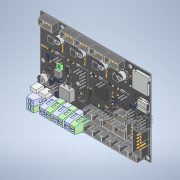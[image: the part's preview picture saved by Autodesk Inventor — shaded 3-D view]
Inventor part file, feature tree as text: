
AUTODESK INVENTOR PART (.ipt)
format: ipt  version: 2022 (Build 260153000, 153)  size: 26,429,440 bytes
history: native  units: in
note: dims shown in document units (in); Inventor stores cm internally (conversion verified against a paired STEP export)
features: other x489, extrude x194, fillet x4
ambient origin geometry x8: Origin, YZ Plane, XZ Plane, XY Plane, X Axis, Y Axis, Z Axis, Center Point
bodies: Solid1 (feature_tree), Solid2 (feature_tree), Solid3 (feature_tree), Solid4 (feature_tree), Solid5 (feature_tree), Solid6 (feature_tree), Solid7 (feature_tree), Solid8 (feature_tree), Solid9 (feature_tree), Solid10 (feature_tree), Solid11 (feature_tree), Solid12 (feature_tree), Solid13 (feature_tree), Solid14 (feature_tree), Solid15 (feature_tree), Solid16 (feature_tree), Solid17 (feature_tree), Solid18 (feature_tree), Solid19 (feature_tree), Solid20 (feature_tree), Solid21 (feature_tree), Solid22 (feature_tree), Solid23 (feature_tree), Solid24 (feature_tree), Solid25 (feature_tree), Solid26 (feature_tree), Solid27 (feature_tree), Solid28 (feature_tree), Solid29 (feature_tree), Solid30 (feature_tree), Solid31 (feature_tree), Solid32 (feature_tree), Solid33 (feature_tree), Solid34 (feature_tree), Solid35 (feature_tree), Solid36 (feature_tree), Solid37 (feature_tree), Solid38 (feature_tree), Solid39 (feature_tree), Solid40 (feature_tree), Solid41 (feature_tree), Solid42 (feature_tree), Solid43 (feature_tree), Solid44 (feature_tree), Solid45 (feature_tree), Solid46 (feature_tree), Solid47 (feature_tree), Solid48 (feature_tree), Solid49 (feature_tree), Solid50 (feature_tree), Solid51 (feature_tree), Solid52 (feature_tree), Solid53 (feature_tree), Solid54 (feature_tree), Solid55 (feature_tree), Solid56 (feature_tree), Solid57 (feature_tree), Solid58 (feature_tree), Solid59 (feature_tree), Solid60 (feature_tree), Solid61 (feature_tree), Solid62 (feature_tree), Solid63 (feature_tree), Solid64 (feature_tree), Solid65 (feature_tree), Solid66 (feature_tree), Solid67 (feature_tree), Solid68 (feature_tree), Solid69 (feature_tree), Solid70 (feature_tree), Solid71 (feature_tree), Solid72 (feature_tree), Solid73 (feature_tree), Solid74 (feature_tree), Solid75 (feature_tree), Solid76 (feature_tree), Solid77 (feature_tree), Solid78 (feature_tree), Solid79 (feature_tree), Solid80 (feature_tree), Solid81 (feature_tree), Solid82 (feature_tree), Solid83 (feature_tree), Solid84 (feature_tree), Solid85 (feature_tree), Solid86 (feature_tree), Solid87 (feature_tree), Solid88 (feature_tree), Solid89 (feature_tree), Solid90 (feature_tree), Solid91 (feature_tree), Solid92 (feature_tree), Solid93 (feature_tree), Solid94 (feature_tree), Solid95 (feature_tree), Solid96 (feature_tree), Solid97 (feature_tree), Solid98 (feature_tree), Solid99 (feature_tree), Solid100 (feature_tree), Solid101 (feature_tree), Solid102 (feature_tree), Solid103 (feature_tree), Solid104 (feature_tree), Solid105 (feature_tree), Solid106 (feature_tree), Solid107 (feature_tree), Solid108 (feature_tree), Solid109 (feature_tree), Solid110 (feature_tree), Solid111 (feature_tree), Solid112 (feature_tree), Solid113 (feature_tree), Solid114 (feature_tree), Solid115 (feature_tree), Solid116 (feature_tree), Solid117 (feature_tree), Solid118 (feature_tree), Solid119 (feature_tree), Solid120 (feature_tree), Solid121 (feature_tree), Solid122 (feature_tree), Solid123 (feature_tree), Solid124 (feature_tree), Solid125 (feature_tree), Solid126 (feature_tree), Solid127 (feature_tree), Solid128 (feature_tree), Solid129 (feature_tree), Solid130 (feature_tree), Solid131 (feature_tree), Solid132 (feature_tree), Solid133 (feature_tree), Solid134 (feature_tree), Solid135 (feature_tree), Solid136 (feature_tree), Solid137 (feature_tree), Solid138 (feature_tree), Solid139 (feature_tree), Solid140 (feature_tree), Solid141 (feature_tree), Solid142 (feature_tree), Solid143 (feature_tree), Solid144 (feature_tree), Solid145 (feature_tree), Solid146 (feature_tree), Solid147 (feature_tree), Solid148 (feature_tree), Solid149 (feature_tree), Solid150 (feature_tree), Solid151 (feature_tree), Solid152 (feature_tree), Solid153 (feature_tree), Solid154 (feature_tree), Solid155 (feature_tree), Solid156 (feature_tree), Solid157 (feature_tree), Solid158 (feature_tree), Solid159 (feature_tree), Solid160 (feature_tree), Solid161 (feature_tree), Solid162 (feature_tree), Solid163 (feature_tree), Solid164 (feature_tree), Solid165 (feature_tree), Solid166 (feature_tree), Solid167 (feature_tree), Solid168 (feature_tree), Solid169 (feature_tree), Solid170 (feature_tree), Solid171 (feature_tree), Solid172 (feature_tree), Solid173 (feature_tree), Solid174 (feature_tree), Solid175 (feature_tree), Solid176 (feature_tree), Solid177 (feature_tree), Solid178 (feature_tree), Solid179 (feature_tree), Solid180 (feature_tree), Solid181 (feature_tree), Solid182 (feature_tree), Solid183 (feature_tree), Solid184 (feature_tree), Solid185 (feature_tree), Solid186 (feature_tree), Solid187 (feature_tree), Solid188 (feature_tree), Solid189 (feature_tree), Solid190 (feature_tree), Solid191 (feature_tree), Solid192 (feature_tree), Solid193 (feature_tree), Solid194 (feature_tree), Solid195 (feature_tree), Solid196 (feature_tree), Solid197 (feature_tree), Solid198 (feature_tree), Solid199 (feature_tree), Solid200 (feature_tree), Solid201 (feature_tree), Solid202 (feature_tree), Solid203 (feature_tree), Solid204 (feature_tree), Solid205 (feature_tree), Solid206 (feature_tree), Solid207 (feature_tree), Solid208 (feature_tree), Solid209 (feature_tree), Solid210 (feature_tree), Solid211 (feature_tree), Solid212 (feature_tree), Solid213 (feature_tree), Solid214 (feature_tree), Solid215 (feature_tree), Solid216 (feature_tree), Solid217 (feature_tree), Solid218 (feature_tree), Solid219 (feature_tree), Solid220 (feature_tree), Solid221 (feature_tree), Solid222 (feature_tree), Solid223 (feature_tree), Solid224 (feature_tree), Solid225 (feature_tree), Solid226 (feature_tree), Solid227 (feature_tree), Solid228 (feature_tree), Solid229 (feature_tree), Solid230 (feature_tree), Solid231 (feature_tree), Solid232 (feature_tree), Solid233 (feature_tree), Solid234 (feature_tree), Solid235 (feature_tree), Solid236 (feature_tree), Solid237 (feature_tree), Solid238 (feature_tree), Solid239 (feature_tree), Solid240 (feature_tree), Solid241 (feature_tree), Solid242 (feature_tree), Solid243 (feature_tree), Solid244 (feature_tree), Solid245 (feature_tree), Solid246 (feature_tree), Solid247 (feature_tree), Solid248 (feature_tree), Solid249 (feature_tree), Solid250 (feature_tree), Solid251 (feature_tree), Solid252 (feature_tree), Solid253 (feature_tree), Solid254 (feature_tree), Solid255 (feature_tree), Solid256 (feature_tree), Solid257 (feature_tree), Solid258 (feature_tree), Solid259 (feature_tree), Solid260 (feature_tree), Solid261 (feature_tree), Solid262 (feature_tree), Solid263 (feature_tree), Solid264 (feature_tree), Solid265 (feature_tree), Solid266 (feature_tree), Solid267 (feature_tree), Solid268 (feature_tree), Solid269 (feature_tree), Solid270 (feature_tree), Solid271 (feature_tree), Solid272 (feature_tree), Solid273 (feature_tree), Solid274 (feature_tree), Solid275 (feature_tree), Solid276 (feature_tree), Solid277 (feature_tree), Solid278 (feature_tree), Solid279 (feature_tree), Solid280 (feature_tree), Solid281 (feature_tree), Solid282 (feature_tree), Solid283 (feature_tree), Solid284 (feature_tree), Solid285 (feature_tree), Solid286 (feature_tree), Solid287 (feature_tree), Solid288 (feature_tree), Solid289 (feature_tree), Solid290 (feature_tree), Solid291 (feature_tree), Solid292 (feature_tree), Solid293 (feature_tree), Solid294 (feature_tree), Solid295 (feature_tree), Solid296 (feature_tree), Solid297 (feature_tree), Solid298 (feature_tree), Solid299 (feature_tree), Solid300 (feature_tree), Solid301 (feature_tree), Solid302 (feature_tree), Solid303 (feature_tree), Solid304 (feature_tree), Solid305 (feature_tree), Solid306 (feature_tree), Solid307 (feature_tree), Solid308 (feature_tree), Solid309 (feature_tree), Solid310 (feature_tree), Solid311 (feature_tree), Solid312 (feature_tree), Solid313 (feature_tree), Solid314 (feature_tree), Solid315 (feature_tree), Solid316 (feature_tree), Solid317 (feature_tree), Solid318 (feature_tree), Solid319 (feature_tree), Solid320 (feature_tree), Solid321 (feature_tree), Solid322 (feature_tree), Solid323 (feature_tree), Solid324 (feature_tree), Solid325 (feature_tree), Solid326 (feature_tree), Solid327 (feature_tree), Solid328 (feature_tree), Solid329 (feature_tree), Solid330 (feature_tree), Solid331 (feature_tree), Solid332 (feature_tree), Solid333 (feature_tree), Solid334 (feature_tree), Solid335 (feature_tree), Solid336 (feature_tree), Solid337 (feature_tree), Solid338 (feature_tree), Solid339 (feature_tree), Solid340 (feature_tree), Solid341 (feature_tree), Solid342 (feature_tree), Solid343 (feature_tree), Solid344 (feature_tree), Solid345 (feature_tree), Solid346 (feature_tree), Solid347 (feature_tree), Solid348 (feature_tree), Solid349 (feature_tree), Solid350 (feature_tree), Solid351 (feature_tree), Solid352 (feature_tree), Solid353 (feature_tree), Solid354 (feature_tree), Solid355 (feature_tree), Solid356 (feature_tree), Solid357 (feature_tree), Solid358 (feature_tree), Solid359 (feature_tree), Solid360 (feature_tree), Solid361 (feature_tree), Solid362 (feature_tree), Solid363 (feature_tree), Solid364 (feature_tree), Solid365 (feature_tree), Solid366 (feature_tree), Solid367 (feature_tree), Solid368 (feature_tree), Solid369 (feature_tree), Solid370 (feature_tree), Solid371 (feature_tree), Solid372 (feature_tree), Solid373 (feature_tree), Solid374 (feature_tree), Solid375 (feature_tree), Solid376 (feature_tree), Solid377 (feature_tree), Solid378 (feature_tree), Solid379 (feature_tree), Solid380 (feature_tree), Solid381 (feature_tree), Solid382 (feature_tree), Solid383 (feature_tree), Solid384 (feature_tree), Solid385 (feature_tree), Solid386 (feature_tree), Solid387 (feature_tree), Solid388 (feature_tree), Solid389 (feature_tree), Solid390 (feature_tree), Solid391 (feature_tree), Solid392 (feature_tree), Solid393 (feature_tree), Solid394 (feature_tree), Solid395 (feature_tree), Solid396 (feature_tree), Solid397 (feature_tree), Solid398 (feature_tree), Solid399 (feature_tree), Solid400 (feature_tree), Solid401 (feature_tree), Solid402 (feature_tree), Solid403 (feature_tree), Solid404 (feature_tree), Solid405 (feature_tree), Solid406 (feature_tree), Solid407 (feature_tree), Solid408 (feature_tree), Solid409 (feature_tree), Solid410 (feature_tree), Solid411 (feature_tree), Solid412 (feature_tree), Solid413 (feature_tree), Solid414 (feature_tree), Solid415 (feature_tree), Solid416 (feature_tree), Solid417 (feature_tree), Solid418 (feature_tree), Solid419 (feature_tree), Solid420 (feature_tree), Solid421 (feature_tree), Solid422 (feature_tree), Solid423 (feature_tree), Solid424 (feature_tree), Solid425 (feature_tree), Solid426 (feature_tree), Solid427 (feature_tree), Solid428 (feature_tree), Solid429 (feature_tree), Solid430 (feature_tree), Solid431 (feature_tree), Solid432 (feature_tree), Solid433 (feature_tree), Solid434 (feature_tree), Solid435 (feature_tree), Solid436 (feature_tree), Solid437 (feature_tree), Solid438 (feature_tree), Solid439 (feature_tree), Solid440 (feature_tree), Solid441 (feature_tree), Solid442 (feature_tree), Solid443 (feature_tree), Solid444 (feature_tree), Solid445 (feature_tree), Solid446 (feature_tree), Solid447 (feature_tree), Solid448 (feature_tree), Solid449 (feature_tree), Solid450 (feature_tree), Solid451 (feature_tree), Solid452 (feature_tree), Solid453 (feature_tree), Solid454 (feature_tree), Solid455 (feature_tree), Solid456 (feature_tree), Solid457 (feature_tree), Solid458 (feature_tree), Solid459 (feature_tree), Solid460 (feature_tree), Solid461 (feature_tree), Solid462 (feature_tree), Solid463 (feature_tree), Solid464 (feature_tree), Solid465 (feature_tree), Solid466 (feature_tree), Solid467 (feature_tree), Solid468 (feature_tree), Solid469 (feature_tree), Solid470 (feature_tree), Solid471 (feature_tree), Solid472 (feature_tree), Solid473 (feature_tree), Solid474 (feature_tree), Solid475 (feature_tree), Solid476 (feature_tree), Solid477 (feature_tree), Solid478 (feature_tree), Solid479 (feature_tree), Solid480 (feature_tree), Solid481 (feature_tree), Solid482 (feature_tree), Solid483 (feature_tree), Solid484 (feature_tree), Solid485 (feature_tree), Solid486 (feature_tree), Solid487 (feature_tree), Solid488 (feature_tree), Solid489 (feature_tree), Solid490 (feature_tree), Solid491 (feature_tree), Solid492 (feature_tree), Solid493 (feature_tree), Solid494 (feature_tree), Solid495 (feature_tree), Solid496 (feature_tree), Solid497 (feature_tree), Solid498 (feature_tree), Solid499 (feature_tree), Solid500 (feature_tree), Solid501 (feature_tree), Solid502 (feature_tree), Solid503 (feature_tree), Solid504 (feature_tree), Solid505 (feature_tree), Solid506 (feature_tree), Solid507 (feature_tree), Solid508 (feature_tree), Solid509 (feature_tree), Solid510 (feature_tree), Solid511 (feature_tree), Solid512 (feature_tree), Solid513 (feature_tree), Solid514 (feature_tree), Solid515 (feature_tree), Solid516 (feature_tree), Solid517 (feature_tree), Solid518 (feature_tree), Solid519 (feature_tree), Solid520 (feature_tree), Solid521 (feature_tree), Solid522 (feature_tree), Solid523 (feature_tree), Solid524 (feature_tree), Solid525 (feature_tree), Solid526 (feature_tree), Solid527 (feature_tree), Solid528 (feature_tree), Solid529 (feature_tree), Solid530 (feature_tree), Solid531 (feature_tree), Solid532 (feature_tree), Solid533 (feature_tree), Solid534 (feature_tree), Solid535 (feature_tree), Solid536 (feature_tree), Solid537 (feature_tree), Solid538 (feature_tree), Solid539 (feature_tree), Solid540 (feature_tree), Solid541 (feature_tree), Solid542 (feature_tree), Solid543 (feature_tree), Solid544 (feature_tree), Solid545 (feature_tree), Solid546 (feature_tree), Solid547 (feature_tree), Solid548 (feature_tree), Solid549 (feature_tree), Solid550 (feature_tree), Solid551 (feature_tree), Solid552 (feature_tree), Solid553 (feature_tree), Solid554 (feature_tree), Solid555 (feature_tree), Solid556 (feature_tree), Solid557 (feature_tree), Solid558 (feature_tree), Solid559 (feature_tree), Solid560 (feature_tree), Solid561 (feature_tree), Solid562 (feature_tree), Solid563 (feature_tree), Solid564 (feature_tree), Solid565 (feature_tree), Solid566 (feature_tree), Solid567 (feature_tree), Solid568 (feature_tree), Solid569 (feature_tree), Solid570 (feature_tree), Solid571 (feature_tree), Solid572 (feature_tree), Solid573 (feature_tree), Solid574 (feature_tree), Solid575 (feature_tree), Solid576 (feature_tree), Solid577 (feature_tree), Solid578 (feature_tree), Solid579 (feature_tree), Solid580 (feature_tree), Solid581 (feature_tree), Solid582 (feature_tree), Solid583 (feature_tree), Solid584 (feature_tree), Solid585 (feature_tree), Solid586 (feature_tree), Solid587 (feature_tree), Solid588 (feature_tree), Solid589 (feature_tree), Solid590 (feature_tree), Solid591 (feature_tree), Solid592 (feature_tree), Solid593 (feature_tree), Solid594 (feature_tree), Solid595 (feature_tree), Solid596 (feature_tree), Solid597 (feature_tree), Solid598 (feature_tree), Solid599 (feature_tree), Solid600 (feature_tree), Solid601 (feature_tree), Solid602 (feature_tree), Solid603 (feature_tree), Solid604 (feature_tree), Solid605 (feature_tree), Solid606 (feature_tree), Solid607 (feature_tree), Solid608 (feature_tree), Solid609 (feature_tree), Solid610 (feature_tree), Solid611 (feature_tree), Solid612 (feature_tree), Solid613 (feature_tree), Solid614 (feature_tree), Solid615 (feature_tree), Solid616 (feature_tree), Solid617 (feature_tree), Solid618 (feature_tree), Solid619 (feature_tree), Solid620 (feature_tree), Solid621 (feature_tree), Solid622 (feature_tree), Solid623 (feature_tree), Solid624 (feature_tree), Solid625 (feature_tree), Solid626 (feature_tree), Solid627 (feature_tree), Solid628 (feature_tree), Solid629 (feature_tree), Solid630 (feature_tree), Solid631 (feature_tree), Solid632 (feature_tree), Solid633 (feature_tree), Solid634 (feature_tree), Solid635 (feature_tree), Solid636 (feature_tree), Solid637 (feature_tree), Solid638 (feature_tree), Solid639 (feature_tree), Solid640 (feature_tree), Solid641 (feature_tree), Solid642 (feature_tree), Solid643 (feature_tree), Solid644 (feature_tree), Solid645 (feature_tree), Solid646 (feature_tree), Solid647 (feature_tree), Solid648 (feature_tree), Solid649 (feature_tree), Solid650 (feature_tree), Solid651 (feature_tree), Solid652 (feature_tree), Solid653 (feature_tree), Solid654 (feature_tree), Solid655 (feature_tree), Solid656 (feature_tree), Solid657 (feature_tree), Solid658 (feature_tree), Solid659 (feature_tree), Solid660 (feature_tree), Solid661 (feature_tree), Solid662 (feature_tree), Solid663 (feature_tree), Solid664 (feature_tree), Solid665 (feature_tree), Solid666 (feature_tree), Solid667 (feature_tree), Solid668 (feature_tree), Solid669 (feature_tree), Solid670 (feature_tree), Solid671 (feature_tree), Solid672 (feature_tree), Solid673 (feature_tree), Solid674 (feature_tree), Solid675 (feature_tree), Solid676 (feature_tree), Solid677 (feature_tree), Solid678 (feature_tree), Solid679 (feature_tree), Solid680 (feature_tree), Solid681 (feature_tree), Solid682 (feature_tree), Solid683 (feature_tree), Solid684 (feature_tree), Solid685 (feature_tree), Solid686 (feature_tree), Solid687 (feature_tree), Solid688 (feature_tree), Solid689 (feature_tree), Solid690 (feature_tree), Solid691 (feature_tree), Solid692 (feature_tree), Solid693 (feature_tree), Solid694 (feature_tree), Solid695 (feature_tree), Solid696 (feature_tree), Solid697 (feature_tree), Solid698 (feature_tree), Solid699 (feature_tree), Solid700 (feature_tree), Solid701 (feature_tree), Solid702 (feature_tree), Solid703 (feature_tree), Solid704 (feature_tree), Solid705 (feature_tree), Solid706 (feature_tree), Solid707 (feature_tree), Solid708 (feature_tree), Solid709 (feature_tree), Solid710 (feature_tree), Solid711 (feature_tree), Solid712 (feature_tree), Solid713 (feature_tree), Solid714 (feature_tree), Solid715 (feature_tree), Solid716 (feature_tree), Solid717 (feature_tree), Solid718 (feature_tree), Solid719 (feature_tree), Solid720 (feature_tree), Solid721 (feature_tree), Solid722 (feature_tree), Solid723 (feature_tree), Solid724 (feature_tree), Solid725 (feature_tree), Solid726 (feature_tree), Solid727 (feature_tree), Solid728 (feature_tree), Solid729 (feature_tree), Solid730 (feature_tree), Solid731 (feature_tree), Solid732 (feature_tree), Solid733 (feature_tree), Solid734 (feature_tree), Solid735 (feature_tree), Solid736 (feature_tree), Solid737 (feature_tree), Solid738 (feature_tree), Solid739 (feature_tree), Solid740 (feature_tree), Solid741 (feature_tree), Solid742 (feature_tree), Solid743 (feature_tree), Solid744 (feature_tree), Solid745 (feature_tree), Solid746 (feature_tree), Solid747 (feature_tree), Solid748 (feature_tree), Solid749 (feature_tree), Solid750 (feature_tree), Solid751 (feature_tree), Solid752 (feature_tree), Solid753 (feature_tree), Solid754 (feature_tree), Solid755 (feature_tree), Solid756 (feature_tree), Solid757 (feature_tree), Solid758 (feature_tree), Solid759 (feature_tree), Solid760 (feature_tree)
feature tree (687):
  other  "Board_1:1"
  other  "KF128_1:1"
  other  "KF128_1:2"
  other  "KF128_1:3"
  other  "KF128_1:4"
  other  "KF128_1:5"
  other  "KF128_1:6"
  other  "KF128_1:7"
  other  "KF128_1:8"
  extrude  "Extruded_1:1"  [1 undecoded]
  extrude  "Extruded (1)_1:1"  [1 undecoded]
  extrude  "Extruded (1)_1:2"  [1 undecoded]
  extrude  "Extruded_1:2"  [1 undecoded]
  extrude  "Extruded (1)_1:3"  [1 undecoded]
  extrude  "Extruded (1)_1:4"  [1 undecoded]
  extrude  "Extruded (2)_1:1"  [1 undecoded]
  extrude  "Extruded (3)_1:1"  [1 undecoded]
  extrude  "Extruded (3)_1:2"  [1 undecoded]
  other  "KF128_2:1"
  other  "KF128_2:2"
  other  "KF128_2:3"
  other  "KF128_2:4"
  other  "KF128_2:5"
  other  "KF128_2:6"
  other  "KF128_2:7"
  other  "KF128_2:8"
  extrude  "Extruded (4)_1:1"  [1 undecoded]
  extrude  "Extruded (5)_1:1"  [1 undecoded]
  extrude  "Extruded (6)_1:1"  [1 undecoded]
  extrude  "Extruded (7)_1:1"  [1 undecoded]
  extrude  "Extruded (8)_1:1"  [1 undecoded]
  other  "Cylinder_1:1"
  other  "Cylinder_1:2"
  other  "Cylinder_1:3"
  other  "Cylinder_1:4"
  extrude  "Extruded (9)_1:1"  [1 undecoded]
  other  "usb_b-c_1:1"
  other  "usb_b-c_1:2"
  other  "usb_b-c_1:3"
  other  "usb_b-c_1:4"
  other  "usb_b-c_1:5"
  other  "usb_b-c_1:6"
  other  "User_Library-XH2_54_2PIN_RGB0_1:1"
  other  "User_Library-XH2_54_2PIN_RGB0_1:2"
  other  "User_Library-XH2_54_2PIN_RGB0_1:3"
  other  "User_Library-XH2_54_2PIN_RGB0_1:4"
  other  "User_Library-XH2_54_2PIN_RGB0_1:5"
  other  "User_Library-XH2_54_2PIN_RGB0_2:1"
  other  "User_Library-XH2_54_2PIN_RGB0_2:2"
  other  "User_Library-XH2_54_2PIN_RGB0_2:3"
  other  "User_Library-XH2_54_2PIN_RGB0_2:4"
  other  "User_Library-XH2_54_2PIN_RGB0_2:5"
  other  "Fusion_1:1"
  other  "Fusion_1:2"
  other  "Fusion_1:3"
  other  "Fusion_1:4"
  other  "Fusion_1:5"
  other  "Fusion_1:6"
  other  "Fusion_1:7"
  other  "Fusion_1:8"
  other  "Fusion_1:9"
  other  "Fusion_1:10"
  other  "Fusion_1:11"
  other  "Fusion_1:12"
  other  "Fusion_1:13"
  other  "Fusion_1:14"
  other  "Fusion_1:15"
  other  "Fusion_1:16"
  other  "Fusion_1:17"
  other  "Fusion_1:18"
  other  "Fusion_1:19"
  other  "Fusion_1:20"
  other  "Fusion_1:21"
  other  "Fusion_1:22"
  other  "Fusion_1:23"
  other  "Fusion_1:24"
  other  "Fusion_1:25"
  other  "Fusion_1:26"
  other  "Fusion_1:27"
  other  "Fusion_1:28"
  other  "Fusion_1:29"
  fillet  "Fillet_1:1"  [1 undecoded]
  other  "Fusion_1:30"
  other  "Fusion_1:31"
  other  "Fusion_1:32"
  other  "Fusion_1:33"
  other  "Fusion_1:34"
  other  "Fusion_1:35"
  other  "Fusion_1:36"
  other  "Fusion_1:37"
  other  "Fusion_1:38"
  other  "Fusion_1:39"
  other  "Fusion_1:40"
  other  "Fusion_1:41"
  other  "Fusion_1:42"
  other  "Fusion_1:43"
  other  "Fusion_1:44"
  other  "Fusion_1:45"
  other  "Fusion_1:46"
  other  "Fusion_1:47"
  other  "Fusion_1:48"
  other  "Fusion_1:49"
  other  "Fusion_1:50"
  other  "Fusion_1:51"
  other  "Fusion_1:52"
  other  "Fusion_1:53"
  other  "Fusion_1:54"
  other  "Fusion_1:55"
  other  "Fusion_1:56"
  other  "Fusion_1:57"
  other  "Fusion_1:58"
  fillet  "Fillet_1:2"  [1 undecoded]
  other  "Fusion_1:59"
  other  "Fusion_1:60"
  other  "Fusion_1:61"
  other  "Fusion_1:62"
  other  "Fusion_1:63"
  other  "Fusion_1:64"
  other  "Fusion_1:65"
  other  "Fusion_1:66"
  other  "Fusion_1:67"
  other  "Fusion_1:68"
  other  "Fusion_1:69"
  other  "Fusion_1:70"
  other  "Fusion_1:71"
  other  "Fusion_1:72"
  other  "Fusion_1:73"
  other  "Fusion_1:74"
  other  "Fusion_1:75"
  other  "Fusion_1:76"
  other  "Fusion_1:77"
  other  "Fusion_1:78"
  other  "Fusion_1:79"
  other  "Fusion_1:80"
  other  "Fusion_1:81"
  other  "Fusion_1:82"
  other  "Fusion_1:83"
  other  "Fusion_1:84"
  other  "Fusion_1:85"
  other  "Fusion_1:86"
  other  "Fusion_1:87"
  fillet  "Fillet_1:3"  [1 undecoded]
  other  "Fusion_1:88"
  other  "Fusion_1:89"
  other  "Fusion_1:90"
  other  "Fusion_1:91"
  other  "Fusion_1:92"
  other  "Fusion_1:93"
  other  "Fusion_1:94"
  other  "Fusion_1:95"
  other  "Fusion_1:96"
  other  "Fusion_1:97"
  other  "Fusion_1:98"
  other  "Fusion_1:99"
  other  "Fusion_1:100"
  other  "Fusion_1:101"
  other  "Fusion_1:102"
  other  "Fusion_1:103"
  other  "Fusion_1:104"
  other  "Fusion_1:105"
  other  "Fusion_1:106"
  other  "Fusion_1:107"
  other  "Fusion_1:108"
  other  "Fusion_1:109"
  other  "Fusion_1:110"
  other  "Fusion_1:111"
  other  "Fusion_1:112"
  other  "Fusion_1:113"
  other  "Fusion_1:114"
  other  "Fusion_1:115"
  other  "Fusion_1:116"
  fillet  "Fillet_1:4"  [1 undecoded]
  other  "Cylinder (1)_1:1"
  other  "Cylinder (1)_1:2"
  other  "Cylinder (1)_1:3"
  extrude  "Extruded (6)_1:2"  [1 undecoded]
  extrude  "Extruded (10)_1:1"  [1 undecoded]
  extrude  "Extruded (11)_1:1"  [1 undecoded]
  extrude  "Extruded (12)_1:1"  [1 undecoded]
  extrude  "Extruded (5)_1:2"  [1 undecoded]
  other  "User_Library-XH2_54_2PIN_RGB0_3:1"
  other  "User_Library-XH2_54_2PIN_RGB0_3:2"
  other  "User_Library-XH2_54_2PIN_RGB0_3:3"
  other  "User_Library-XH2_54_2PIN_RGB0_3:4"
  other  "User_Library-XH2_54_2PIN_RGB0_3:5"
  other  "User_Library-XH2_54_2PIN_RGB0_4:1"
  other  "User_Library-XH2_54_2PIN_RGB0_4:2"
  other  "User_Library-XH2_54_2PIN_RGB0_4:3"
  other  "User_Library-XH2_54_2PIN_RGB0_4:4"
  other  "User_Library-XH2_54_2PIN_RGB0_4:5"
  other  "User_Library-XH2_54_2PIN_RGB0_5:1"
  other  "User_Library-XH2_54_2PIN_RGB0_5:2"
  other  "User_Library-XH2_54_2PIN_RGB0_5:3"
  other  "User_Library-XH2_54_2PIN_RGB0_5:4"
  other  "User_Library-XH2_54_2PIN_RGB0_5:5"
  extrude  "Extruded (13)_1:1"  [1 undecoded]
  other  "User_Library-XH2_54_2PIN_RGB0_6:1"
  other  "User_Library-XH2_54_2PIN_RGB0_6:2"
  other  "User_Library-XH2_54_2PIN_RGB0_6:3"
  other  "User_Library-XH2_54_2PIN_RGB0_6:4"
  other  "User_Library-XH2_54_2PIN_RGB0_6:5"
  other  "Cylinder (1)_1:4"
  other  "Cylinder (1)_1:5"
  other  "Cylinder (1)_1:6"
  extrude  "Extruded (6)_1:3"  [1 undecoded]
  extrude  "Extruded (10)_1:2"  [1 undecoded]
  extrude  "Extruded (11)_1:2"  [1 undecoded]
  extrude  "Extruded (12)_1:2"  [1 undecoded]
  extrude  "Extruded (5)_1:3"  [1 undecoded]
  other  "User_Library-led_0805_1:1"
  extrude  "Extruded_1:3"  [1 undecoded]
  extrude  "Extruded (1)_1:5"  [1 undecoded]
  extrude  "Extruded (1)_1:6"  [1 undecoded]
  other  "TQFP-64_10x10_1:1"
  other  "User_Library-XH2_54_2PIN_RGB0_7:1"
  other  "User_Library-XH2_54_2PIN_RGB0_7:2"
  other  "User_Library-XH2_54_2PIN_RGB0_7:3"
  other  "User_Library-XH2_54_2PIN_RGB0_7:4"
  other  "User_Library-XH2_54_2PIN_RGB0_7:5"
  extrude  "Extruded (4)_1:2"  [1 undecoded]
  extrude  "Extruded (5)_1:4"  [1 undecoded]
  extrude  "Extruded (6)_1:4"  [1 undecoded]
  extrude  "Extruded (7)_1:2"  [1 undecoded]
  extrude  "Extruded (8)_1:2"  [1 undecoded]
  other  "Cylinder_1:5"
  other  "Cylinder_1:6"
  other  "Cylinder_1:7"
  other  "Cylinder_1:8"
  other  "R0603_1:1"
  other  "R0603_1:2"
  other  "R0603_2:1"
  other  "R0603_2:2"
  other  "R0603_3:1"
  other  "R0603_3:2"
  other  "R0603_4:1"
  other  "R0603_4:2"
  other  "R0603_5:1"
  other  "R0603_5:2"
  other  "R0603_6:1"
  other  "R0603_6:2"
  other  "R0603_7:1"
  other  "R0603_7:2"
  other  "R0603_8:1"
  other  "R0603_8:2"
  other  "R0603_9:1"
  other  "R0603_9:2"
  other  "R0603_10:1"
  other  "R0603_10:2"
  other  "R0603_11:1"
  other  "R0603_11:2"
  other  "R0603_12:1"
  other  "R0603_12:2"
  other  "User_Library-LED_0603_G_Pad004_1:1"
  other  "User_Library-LED_0603_G_Fillet_1:1"
  other  "User_Library-LED_0603_G_Pocket001_1:1"
  other  "User_Library-LED_0603_G_Pad_1:1"
  other  "User_Library-LED_0603_G_Pad004_1:2"
  other  "User_Library-LED_0603_G_Fillet_1:2"
  other  "User_Library-LED_0603_G_Pocket001_1:2"
  other  "User_Library-LED_0603_G_Pad_1:2"
  other  "TSSOP-8_1:1"
  other  "TSSOP-8_1:2"
  other  "TSSOP-8_1:3"
  other  "TSSOP-8_1:4"
  other  "TSSOP-8_1:5"
  other  "TSSOP-8_1:6"
  other  "TSSOP-8_1:7"
  other  "TSSOP-8_1:8"
  other  "TSSOP-8_1:9"
  other  "SO-8_1:1"
  other  "SO-8_1:2"
  other  "SO-8_1:3"
  other  "SO-8_1:4"
  other  "SO-8_1:5"
  other  "SO-8_1:6"
  other  "SO-8_1:7"
  other  "SO-8_1:8"
  other  "SO-8_1:9"
  other  "R0603_13:1"
  other  "R0603_13:2"
  other  "R0603_14:1"
  other  "R0603_14:2"
  other  "R0603_15:1"
  other  "R0603_15:2"
  other  "R0603_16:1"
  other  "R0603_16:2"
  other  "R0603_17:1"
  other  "R0603_17:2"
  other  "R0603_18:1"
  other  "R0603_18:2"
  other  "R0603_19:1"
  other  "R0603_19:2"
  other  "R0603_20:1"
  other  "R0603_20:2"
  other  "R0603_21:1"
  other  "R0603_21:2"
  other  "R0603_22:1"
  other  "R0603_22:2"
  other  "R0603_23:1"
  other  "R0603_23:2"
  extrude  "Extruded (14)_1:1"  [1 undecoded]
  extrude  "Extruded (15)_1:1"  [1 undecoded]
  extrude  "Extruded (16)_1:1"  [1 undecoded]
  extrude  "Extruded (17)_1:1"  [1 undecoded]
  other  "Cylinder (2)_1:1"
  other  "Cylinder (2)_1:2"
  other  "Cylinder (2)_1:3"
  other  "Cylinder (2)_1:4"
  extrude  "Extruded (18)_1:1"  [1 undecoded]
  other  "Cylinder (3)_1:1"
  other  "DO214AC-SMA_S1G_1:1"
  extrude  "Extruded (2)_1:2"  [1 undecoded]
  extrude  "Extruded (3)_1:3"  [1 undecoded]
  extrude  "Extruded (3)_1:4"  [1 undecoded]
  other  "User_Library-0805_SMD_Capacitor_1:1"
  extrude  "Extruded (2)_1:3"  [1 undecoded]
  extrude  "Extruded (3)_1:5"  [1 undecoded]
  extrude  "Extruded (3)_1:6"  [1 undecoded]
  extrude  "Extruded_1:4"  [1 undecoded]
  extrude  "Extruded (1)_1:7"  [1 undecoded]
  extrude  "Extruded (1)_1:8"  [1 undecoded]
  other  "R0603_24:1"
  other  "R0603_24:2"
  other  "R0603_25:1"
  other  "R0603_25:2"
  extrude  "Extruded_1:5"  [1 undecoded]
  extrude  "Extruded (1)_1:9"  [1 undecoded]
  extrude  "Extruded (1)_1:10"  [1 undecoded]
  extrude  "Extruded (19)_1:1"  [1 undecoded]
  extrude  "Extruded (20)_1:1"  [1 undecoded]
  extrude  "Extruded (19)_1:2"  [1 undecoded]
  extrude  "Extruded (2)_1:4"  [1 undecoded]
  extrude  "Extruded (3)_1:7"  [1 undecoded]
  extrude  "Extruded (3)_1:8"  [1 undecoded]
  extrude  "Extruded (2)_1:5"  [1 undecoded]
  extrude  "Extruded (3)_1:9"  [1 undecoded]
  extrude  "Extruded (3)_1:10"  [1 undecoded]
  other  "SL-E_1:1"
  extrude  "Extruded (2)_1:6"  [1 undecoded]
  extrude  "Extruded (3)_1:11"  [1 undecoded]
  extrude  "Extruded (3)_1:12"  [1 undecoded]
  extrude  "Extruded (2)_1:7"  [1 undecoded]
  extrude  "Extruded (3)_1:13"  [1 undecoded]
  extrude  "Extruded (3)_1:14"  [1 undecoded]
  extrude  "Extruded (2)_1:8"  [1 undecoded]
  extrude  "Extruded (3)_1:15"  [1 undecoded]
  extrude  "Extruded (3)_1:16"  [1 undecoded]
  extrude  "Extruded (2)_1:9"  [1 undecoded]
  extrude  "Extruded (3)_1:17"  [1 undecoded]
  extrude  "Extruded (3)_1:18"  [1 undecoded]
  extrude  "Extruded_1:6"  [1 undecoded]
  extrude  "Extruded (1)_1:11"  [1 undecoded]
  extrude  "Extruded (1)_1:12"  [1 undecoded]
  extrude  "Extruded_1:7"  [1 undecoded]
  extrude  "Extruded (1)_1:13"  [1 undecoded]
  extrude  "Extruded (1)_1:14"  [1 undecoded]
  other  "User_Library-0805_SMD_Capacitor_2:1"
  extrude  "Extruded_1:8"  [1 undecoded]
  extrude  "Extruded (1)_1:15"  [1 undecoded]
  extrude  "Extruded (1)_1:16"  [1 undecoded]
  extrude  "Extruded (2)_1:10"  [1 undecoded]
  extrude  "Extruded (3)_1:19"  [1 undecoded]
  extrude  "Extruded (3)_1:20"  [1 undecoded]
  extrude  "Extruded_1:9"  [1 undecoded]
  extrude  "Extruded (1)_1:17"  [1 undecoded]
  extrude  "Extruded (1)_1:18"  [1 undecoded]
  extrude  "Extruded (2)_1:11"  [1 undecoded]
  extrude  "Extruded (3)_1:21"  [1 undecoded]
  extrude  "Extruded (3)_1:22"  [1 undecoded]
  other  "SL-E_2:1"
  extrude  "Extruded_1:10"  [1 undecoded]
  extrude  "Extruded (1)_1:19"  [1 undecoded]
  extrude  "Extruded (1)_1:20"  [1 undecoded]
  other  "User_Library-0805_SMD_Capacitor_3:1"
  extrude  "Extruded (2)_1:12"  [1 undecoded]
  extrude  "Extruded (3)_1:23"  [1 undecoded]
  extrude  "Extruded (3)_1:24"  [1 undecoded]
  extrude  "Extruded_1:11"  [1 undecoded]
  extrude  "Extruded (1)_1:21"  [1 undecoded]
  extrude  "Extruded (1)_1:22"  [1 undecoded]
  other  "User_Library-led_0805_2:1"
  other  "User_Library-LED_0603_G_Pad004_1:3"
  other  "User_Library-LED_0603_G_Fillet_1:3"
  other  "User_Library-LED_0603_G_Pocket001_1:3"
  other  "User_Library-LED_0603_G_Pad_1:3"
  other  "User_Library-LED_0603_G_Pad004_1:4"
  other  "User_Library-LED_0603_G_Fillet_1:4"
  other  "User_Library-LED_0603_G_Pocket001_1:4"
  other  "User_Library-LED_0603_G_Pad_1:4"
  other  "User_Library-XH2_54_2PIN_RGB0_8:1"
  other  "User_Library-XH2_54_2PIN_RGB0_8:2"
  other  "User_Library-XH2_54_2PIN_RGB0_8:3"
  other  "User_Library-XH2_54_2PIN_RGB0_8:4"
  other  "User_Library-XH2_54_2PIN_RGB0_8:5"
  other  "KF128_3:1"
  other  "KF128_3:2"
  other  "KF128_3:3"
  other  "KF128_3:4"
  other  "KF128_3:5"
  other  "KF128_3:6"
  other  "KF128_3:7"
  other  "KF128_3:8"
  other  "R0805_1:1"
  other  "R0805_1:2"
  other  "TO-252_1:1"
  other  "R0603_26:1"
  other  "R0603_26:2"
  other  "R0603_27:1"
  other  "R0603_27:2"
  other  "R0603_28:1"
  other  "R0603_28:2"
  other  "R0603_29:1"
  other  "R0603_29:2"
  other  "R0603_30:1"
  other  "R0603_30:2"
  other  "R0603_31:1"
  other  "R0603_31:2"
  other  "R0603_32:1"
  other  "R0603_32:2"
  other  "R0603_33:1"
  other  "R0603_33:2"
  other  "R0603_34:1"
  other  "R0603_34:2"
  other  "R0603_35:1"
  other  "R0603_35:2"
  other  "R0603_36:1"
  other  "R0603_36:2"
  other  "R0603_37:1"
  other  "R0603_37:2"
  other  "R0603_38:1"
  other  "R0603_38:2"
  other  "R0603_39:1"
  other  "R0603_39:2"
  other  "R0603_40:1"
  other  "R0603_40:2"
  other  "R0603_41:1"
  other  "R0603_41:2"
  other  "R0603_42:1"
  other  "R0603_42:2"
  other  "R0603_43:1"
  other  "R0603_43:2"
  other  "R0603_44:1"
  other  "R0603_44:2"
  other  "R0603_45:1"
  other  "R0603_45:2"
  other  "R0603_46:1"
  other  "R0603_46:2"
  other  "R0603_47:1"
  other  "R0603_47:2"
  other  "R0603_48:1"
  other  "R0603_48:2"
  other  "User_Library-R-0603-Array-4-1_1:1"
  other  "User_Library-R-0603-Array-4-1_2:1"
  other  "User_Library-R-0603-Array-4-1_3:1"
  other  "User_Library-R-0603-Array-4-1_4:1"
  other  "SOT-223_MP04A_1:1"
  other  "SOT-223_MP04A_1:2"
  other  "SOT-223_MP04A_1:3"
  other  "SOT-223_MP04A_1:4"
  other  "SOT-223_MP04A_1:5"
  other  "SOT-223_MP04A_1:6"
  other  "DO214AC-SMA_S1G_2:1"
  other  "DO214AC-SMA_S1G_3:1"
  other  "R0603_49:1"
  other  "R0603_49:2"
  other  "User_Library-GeyerElectronics_KX7_1:1"
  other  "User_Library-GeyerElectronics_KX7_1:2"
  other  "User_Library-GeyerElectronics_KX7_1:3"
  other  "User_Library-GeyerElectronics_KX7_1:4"
  extrude  "Extruded (21)_1:1"  [1 undecoded]
  other  "User_Library-LED_0603_G_Pad004_1:5"
  other  "User_Library-LED_0603_G_Fillet_1:5"
  other  "User_Library-LED_0603_G_Pocket001_1:5"
  other  "User_Library-LED_0603_G_Pad_1:5"
  other  "R0603_50:1"
  other  "R0603_50:2"
  other  "R0603_51:1"
  other  "R0603_51:2"
  other  "R0603_52:1"
  other  "R0603_52:2"
  other  "R0603_53:1"
  other  "R0603_53:2"
  extrude  "Extruded (22)_1:1"  [1 undecoded]
  extrude  "Extruded (23)_1:1"  [1 undecoded]
  other  "Cylinder (4)_1:1"
  other  "Cylinder (4)_1:2"
  other  "Cylinder (4)_1:3"
  other  "Cylinder (4)_1:4"
  other  "Cylinder (4)_1:5"
  other  "Cylinder (4)_1:6"
  other  "Cylinder (4)_1:7"
  other  "Cylinder (4)_1:8"
  other  "Cylinder (4)_1:9"
  other  "Cylinder (4)_1:10"
  extrude  "Extruded (2)_1:13"  [1 undecoded]
  extrude  "Extruded (3)_1:25"  [1 undecoded]
  extrude  "Extruded (3)_1:26"  [1 undecoded]
  extrude  "Extruded_1:12"  [1 undecoded]
  extrude  "Extruded (1)_1:23"  [1 undecoded]
  extrude  "Extruded (1)_1:24"  [1 undecoded]
  extrude  "Extruded (2)_1:14"  [1 undecoded]
  extrude  "Extruded (3)_1:27"  [1 undecoded]
  extrude  "Extruded (3)_1:28"  [1 undecoded]
  other  "SL-E_3:1"
  extrude  "Extruded (2)_1:15"  [1 undecoded]
  extrude  "Extruded (3)_1:29"  [1 undecoded]
  extrude  "Extruded (3)_1:30"  [1 undecoded]
  extrude  "Extruded_1:13"  [1 undecoded]
  extrude  "Extruded (1)_1:25"  [1 undecoded]
  extrude  "Extruded (1)_1:26"  [1 undecoded]
  extrude  "Extruded (2)_1:16"  [1 undecoded]
  extrude  "Extruded (3)_1:31"  [1 undecoded]
  extrude  "Extruded (3)_1:32"  [1 undecoded]
  extrude  "Extruded (2)_1:17"  [1 undecoded]
  extrude  "Extruded (3)_1:33"  [1 undecoded]
  extrude  "Extruded (3)_1:34"  [1 undecoded]
  extrude  "Extruded (2)_1:18"  [1 undecoded]
  extrude  "Extruded (3)_1:35"  [1 undecoded]
  extrude  "Extruded (3)_1:36"  [1 undecoded]
  extrude  "Extruded (2)_1:19"  [1 undecoded]
  extrude  "Extruded (3)_1:37"  [1 undecoded]
  extrude  "Extruded (3)_1:38"  [1 undecoded]
  other  "SL-E_4:1"
  extrude  "Extruded (2)_1:20"  [1 undecoded]
  extrude  "Extruded (3)_1:39"  [1 undecoded]
  extrude  "Extruded (3)_1:40"  [1 undecoded]
  extrude  "Extruded_1:14"  [1 undecoded]
  extrude  "Extruded (1)_1:27"  [1 undecoded]
  extrude  "Extruded (1)_1:28"  [1 undecoded]
  extrude  "Extruded_1:15"  [1 undecoded]
  extrude  "Extruded (1)_1:29"  [1 undecoded]
  extrude  "Extruded (1)_1:30"  [1 undecoded]
  extrude  "Extruded (2)_1:21"  [1 undecoded]
  extrude  "Extruded (3)_1:41"  [1 undecoded]
  extrude  "Extruded (3)_1:42"  [1 undecoded]
  extrude  "Extruded_1:16"  [1 undecoded]
  extrude  "Extruded (1)_1:31"  [1 undecoded]
  extrude  "Extruded (1)_1:32"  [1 undecoded]
  other  "User_Library-0805_SMD_Capacitor_4:1"
  extrude  "Extruded (2)_1:22"  [1 undecoded]
  extrude  "Extruded (3)_1:43"  [1 undecoded]
  extrude  "Extruded (3)_1:44"  [1 undecoded]
  other  "SL-E_5:1"
  extrude  "Extruded (2)_1:23"  [1 undecoded]
  extrude  "Extruded (3)_1:45"  [1 undecoded]
  extrude  "Extruded (3)_1:46"  [1 undecoded]
  extrude  "Extruded_1:17"  [1 undecoded]
  extrude  "Extruded (1)_1:33"  [1 undecoded]
  extrude  "Extruded (1)_1:34"  [1 undecoded]
  extrude  "Extruded_1:18"  [1 undecoded]
  extrude  "Extruded (1)_1:35"  [1 undecoded]
  extrude  "Extruded (1)_1:36"  [1 undecoded]
  extrude  "Extruded (2)_1:24"  [1 undecoded]
  extrude  "Extruded (3)_1:47"  [1 undecoded]
  extrude  "Extruded (3)_1:48"  [1 undecoded]
  extrude  "Extruded_1:19"  [1 undecoded]
  extrude  "Extruded (1)_1:37"  [1 undecoded]
  extrude  "Extruded (1)_1:38"  [1 undecoded]
  extrude  "Extruded_1:20"  [1 undecoded]
  extrude  "Extruded (1)_1:39"  [1 undecoded]
  extrude  "Extruded (1)_1:40"  [1 undecoded]
  extrude  "Extruded (4)_1:3"  [1 undecoded]
  extrude  "Extruded (5)_1:5"  [1 undecoded]
  extrude  "Extruded (6)_1:5"  [1 undecoded]
  extrude  "Extruded (7)_1:3"  [1 undecoded]
  extrude  "Extruded (8)_1:3"  [1 undecoded]
  other  "Cylinder_1:9"
  other  "Cylinder_1:10"
  other  "Cylinder_1:11"
  other  "Cylinder_1:12"
  other  "TO263_1:1"
  other  "R0603_54:1"
  other  "R0603_54:2"
  other  "R0805_2:1"
  other  "R0805_2:2"
  other  "R0603_55:1"
  other  "R0603_55:2"
  other  "R0805_3:1"
  other  "R0805_3:2"
  other  "R0603_56:1"
  other  "R0603_56:2"
  other  "R0603_57:1"
  other  "R0603_57:2"
  other  "R0805_4:1"
  other  "R0805_4:2"
  other  "R0603_58:1"
  other  "R0603_58:2"
  other  "R0805_5:1"
  other  "R0805_5:2"
  other  "R0603_59:1"
  other  "R0603_59:2"
  other  "R0603_60:1"
  other  "R0603_60:2"
  other  "R0603_61:1"
  other  "R0603_61:2"
  other  "R0603_62:1"
  other  "R0603_62:2"
  other  "R0805_6:1"
  other  "R0805_6:2"
  other  "R0603_63:1"
  other  "R0603_63:2"
  other  "R0805_7:1"
  other  "R0805_7:2"
  other  "R0603_64:1"
  other  "R0603_64:2"
  other  "R0603_65:1"
  other  "R0603_65:2"
  other  "R0603_66:1"
  other  "R0603_66:2"
  other  "R0603_67:1"
  other  "R0603_67:2"
  other  "R0603_68:1"
  other  "R0603_68:2"
  other  "R0603_69:1"
  other  "R0603_69:2"
  other  "R0603_70:1"
  other  "R0603_70:2"
  other  "R0805_8:1"
  other  "R0805_8:2"
  other  "R0603_71:1"
  other  "R0603_71:2"
  other  "R0805_9:1"
  other  "R0805_9:2"
  other  "R0603_72:1"
  other  "R0603_72:2"
  other  "TSSOP14-1_1:1"
  other  "TSSOP14-1_1:2"
  other  "TSSOP14-1_1:3"
  other  "TSSOP14-1_1:4"
  other  "TSSOP14-1_1:5"
  other  "TSSOP14-1_1:6"
  other  "TSSOP14-1_1:7"
  other  "TSSOP14-1_1:8"
  other  "SOT-23-5_1:1"
  other  "SOT-23-5_1:2"
  other  "SOT-23-5_1:3"
  other  "SOT-23-5_1:4"
  other  "SOT-23-5_1:5"
  other  "SOT-23-5_1:6"
  other  "SOT-23-5_1:7"
  extrude  "Extruded (4)_1:4"  [1 undecoded]
  extrude  "Extruded (5)_1:6"  [1 undecoded]
  extrude  "Extruded (6)_1:6"  [1 undecoded]
  extrude  "Extruded (7)_1:4"  [1 undecoded]
  extrude  "Extruded (8)_1:4"  [1 undecoded]
  other  "Cylinder_1:13"
  other  "Cylinder_1:14"
  other  "Cylinder_1:15"
  other  "Cylinder_1:16"
  extrude  "Extruded (4)_1:5"  [1 undecoded]
  extrude  "Extruded (5)_1:7"  [1 undecoded]
  extrude  "Extruded (6)_1:7"  [1 undecoded]
  extrude  "Extruded (7)_1:5"  [1 undecoded]
  extrude  "Extruded (8)_1:5"  [1 undecoded]
  other  "Cylinder_1:17"
  other  "Cylinder_1:18"
  other  "Cylinder_1:19"
  other  "Cylinder_1:20"
  other  "KF128_4:1"
  other  "KF128_4:2"
  other  "KF128_4:3"
  other  "KF128_4:4"
  other  "KF128_4:5"
  other  "KF128_4:6"
  other  "KF128_4:7"
  other  "KF128_4:8"
  other  "DO214AC-SMA_S1G_4:1"
  other  "Fuse_1812_1:1"
  other  "Cylinder (1)_1:7"
  other  "Cylinder (1)_1:8"
  other  "Cylinder (1)_1:9"
  extrude  "Extruded (6)_1:8"  [1 undecoded]
  extrude  "Extruded (10)_1:3"  [1 undecoded]
  extrude  "Extruded (11)_1:3"  [1 undecoded]
  extrude  "Extruded (12)_1:3"  [1 undecoded]
  extrude  "Extruded (5)_1:8"  [1 undecoded]
  extrude  "Extruded_1:21"  [1 undecoded]
  extrude  "Extruded (1)_1:41"  [1 undecoded]
  extrude  "Extruded (1)_1:42"  [1 undecoded]
  extrude  "Extruded_1:22"  [1 undecoded]
  extrude  "Extruded (1)_1:43"  [1 undecoded]
  extrude  "Extruded (1)_1:44"  [1 undecoded]
  extrude  "Extruded_1:23"  [1 undecoded]
  extrude  "Extruded (1)_1:45"  [1 undecoded]
  extrude  "Extruded (1)_1:46"  [1 undecoded]
  other  "Composite1"
  other  "Srf1"
note: 198 required parameter values undecoded (feature->parameter linkage not recoverable at this tier; creation-order binding heuristic only, values carry confidence <= 0.55)
